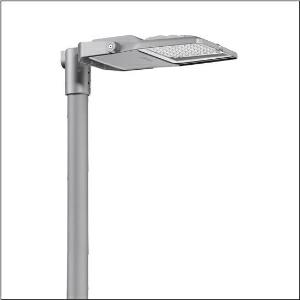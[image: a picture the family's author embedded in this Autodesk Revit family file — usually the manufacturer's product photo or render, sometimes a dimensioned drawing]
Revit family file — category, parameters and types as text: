
# Revit family: floodlight_fl_21_iq_mini___pl52_5xa7771c4d3a_e4a2
name_source: partatom
category: Lighting Fixtures
units: mm (PartAtom-declared; Revit-internal decimal feet)

## family parameters
Cut with Voids When Loaded = No
Host = Face
Light Source = No
Part Type = Normal
Room Calculation Point = No
Round Connector Dimension = Use Diameter
Shared = No

## types (1)
- --- (1 x LED, 12720 lm, 87.2 W, 4000K)
    Apparent Load = 87 VA
    CIE Flux Codes = 26 60 98 100 100
    Color Rendering = 70
    Color Temperature = 4000K
    Default Elevation = 1800 mm
    Description = Floodlight FL 21 iQ mini, floodlight, primary light control with lens, of PMMA, primary optical cover: protective disc, of toughened safety glass, transparent, light distribution: PL52, light emission: direct distribution, installation type: surface-mounted, LED, High Power LED, rated luminous flux: 12.720lm, luminous efficacy: 146lm/W, light colour: 740, colour temperature: 4000K, control: Auto-Match, Temp-Guard, Lumen-Switch, Night-Set, Smart-Wire, Light-Fading, Desk-Remote (wireless, voltage-free reading and setting of iQ features in the workshop via application-optimized NFC function/RFID function), optimised constant luminous flux control (CLO 2.0), with terminal, 6-pole, mains connection: 220..240V, AC, 50/60Hz, start of lifetime: 87W, end of service life: 92W, reduction: 40W, luminaire housing, of diecast aluminium, powder-coated, Siteco® metallic grey (DB 702S), corrosivity category C5 mid according to DIN EN ISO 12944, sealing non-destructively replaceable, please order mast flange separately, mast bracket, of steel, galvanised, powder-coated, Siteco® metallic grey (DB 702S), protection rating (complete): IP66, insulation class (complete): insulation class II (safety insulation), certification: CE, ENEC, VDE, protection symbol: D, impact resistance: IK08, permissible operating ambient temperature: -40..+40°C, permissible operating ambient temperature for outdoor applications: -40..+50°C, standard: DIN EN 12944, LABS conformity tested according to VDMA 24364:2018-05, packaging unit: 1 piece

Light Distribution: PL52
    Height = 70 mm
    Lamp = 1 x LED
    Lamp Light Flux = 12720 lm
    Lamp Power = 87.2 W
    Lamp count = 1
    Length = 485 mm
    Luminous efficacy = 146 lm/W
    Manufacturer = Siteco
    ModVariant = No
    Model = 5XA7771C4D3A
    Number of Poles = 1
    OnlyDefault = Yes
    Power Factor = 1
    Product Name = Floodlight FL 21 iQ mini | PL52
    Product group = floodlight | pylon annexe
    ProductGroupID = 6200
    Protection Class = Protection class II
    Protection Degree = IP 66
    RLX_Detail_Level = 1
    RLX_Emergency_Light_Flux = 0 lm
    RLX_Emergency_Type = 0
    RLX_Emergency_Type_DB = No
    RlxData = <blob elided: 101473 chars, md5=4ed54671>
    Socket = socket
    Standby Power = 0 W
    System Light Flux = 12720 lm
    System Power = 87 W
    Type Comments = factory setting: luminous flux: 100 % | dim-lin: 254 | 456 mA
    Type Image = l_1007125.jpg
    URL = http://relux.com
    VarID = @adj_134781
    Voltage = 0 V
    Weight = 0.00 kg
    Width = 337 mm

## geometry (parser evidence)
native form markers: Blend x4, Sweep x12
no freeform markers — native parametric forms only
